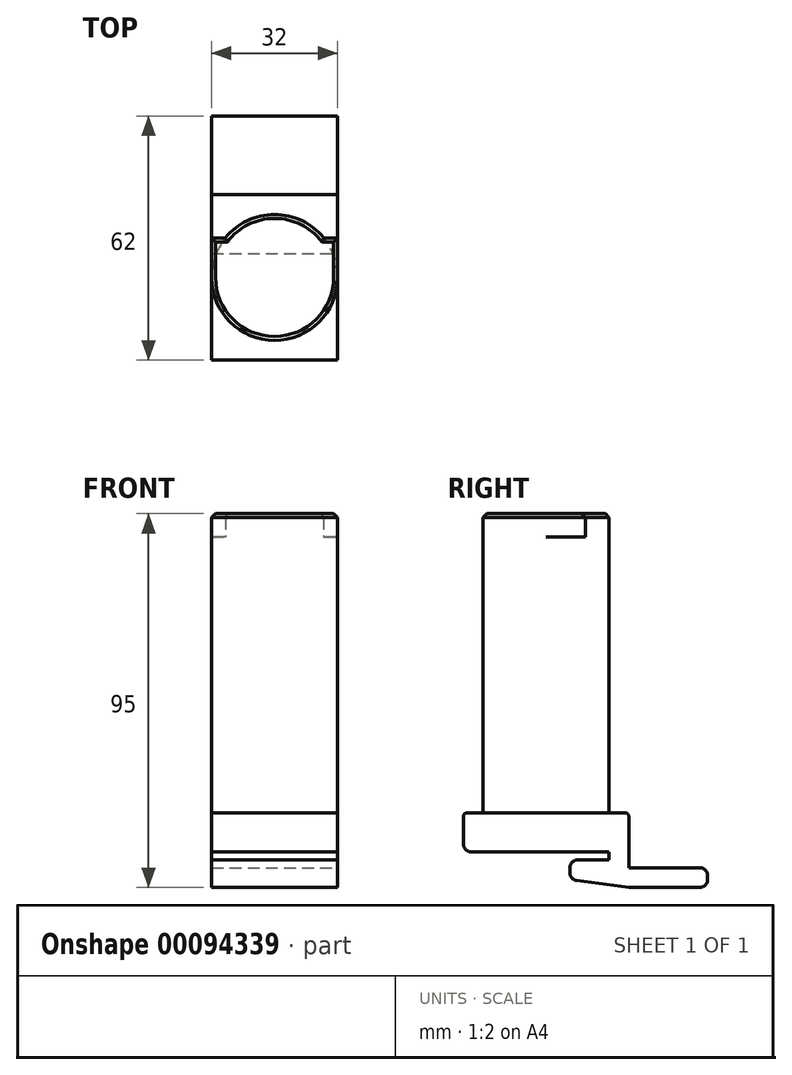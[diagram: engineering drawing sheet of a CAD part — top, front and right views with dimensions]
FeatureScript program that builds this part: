
annotation { "Feature Type Name" : "Feature", "Feature Type Description" : "" }
export const myFeature = defineFeature(function(context is Context, id is Id, definition is map)
    precondition{}
    {
        {
            var Q0;
            Q0=qCreatedBy(makeId("Top.planeOp"),FACE);
            var sketch = newSketch(context, id + "F0", { "sketchPlane" : qUnion([Q0])});
            skCircle(sketch, "E0", {"center": v(0, 0) * mm, "radius": 16 * mm});
            skLineSegment(sketch, "E1.bottom", {"start": v(-16, -21) * mm, "end": v(16, -21) * mm});
            skLineSegment(sketch, "E1.top", {"start": v(-16, 21) * mm, "end": v(16, 21) * mm});
            skLineSegment(sketch, "E1.left", {"start": v(-16, -21) * mm, "end": v(-16, 21) * mm});
            skLineSegment(sketch, "E1.right", {"start": v(16, -21) * mm, "end": v(16, 21) * mm});
            skSolve(sketch);
        }
        {
            var Q0;
            Q0=makeQuery(id+"F0.imprint","IMPRINT",FACE,{"disambiguationData":[TD([[makeQuery(id+"F0.imprint","IMPRINT",EDGE,{"derivedFrom":sQuery(id+"F0.wireOp",EDGE,"E0")}),1.0]])]});
            extrude(context, id + "F1", {"entities" : qUnion([Q0]), "depth" : 70 * mm});
        }
        {
            var Q0;
            Q0=makeQuery(id+"F1.opExtrude","CAP_FACE",FACE,{"disambiguationData":[OSD([sQuery(id+"F0.wireOp",EDGE,"E0")])],"isStart":false});
            var sketch = newSketch(context, id + "F2", { "sketchPlane" : qUnion([Q0])});
            skLineSegment(sketch, "E2", {"start": v(-16, 0) * mm, "end": v(-16, 10) * mm});
            skLineSegment(sketch, "E3", {"start": v(16, 0) * mm, "end": v(16, 10) * mm});
            skLineSegment(sketch, "E4", {"start": v(-16, 10) * mm, "end": v(16, 10) * mm});
            skPoint(sketch, "E5", {"position": v(0, 10) * mm});
            skArc(sketch, "E6", {"start": v(-16, 10) * mm, "mid": v(0, 26) * mm, "end": v(16, 10) * mm});
            skSolve(sketch);
        }
        {
            var Q0;
            {var subQ0=sQuery(id+"F2.wireOp",EDGE,"E6");Q0=makeQuery(id+"F2.imprint","IMPRINT",FACE,{"disambiguationData":[TD([[makeQuery(id+"F2.imprint","IMPRINT",EDGE,{"derivedFrom":subQ0}),-1.0]])]});}
            var Q1;
            {var subQ0=sQuery(id+"F2.wireOp",EDGE,"E4");var subQ1=makeQuery(id+"F1.opExtrude","CAP_EDGE",EDGE,{"disambiguationData":[OSD([sQuery(id+"F0.wireOp",EDGE,"E0")])],"isStart":false});var subQ2=makeQuery(id+"F2.imprint","INTERSECT",VERTEX,{"disambiguationData":[OD(0.0)],"derivedFrom":[subQ1,subQ0]});Q1=makeQuery(id+"F2.imprint","IMPRINT",FACE,{"disambiguationData":[TD([[makeQuery(id+"F2.imprint","IMPRINT",EDGE,{"disambiguationData":[TD([[subQ2,-1.0]])],"derivedFrom":subQ0}),1.0]])]});}
            var Q2;
            {var subQ0=sQuery(id+"F2.wireOp",EDGE,"E2");Q2=makeQuery(id+"F2.imprint","IMPRINT",FACE,{"disambiguationData":[TD([[makeQuery(id+"F2.imprint","IMPRINT",EDGE,{"derivedFrom":subQ0}),-1.0]])]});}
            var Q3;
            {var subQ0=sQuery(id+"F2.wireOp",EDGE,"E3");Q3=makeQuery(id+"F2.imprint","IMPRINT",FACE,{"disambiguationData":[TD([[makeQuery(id+"F2.imprint","IMPRINT",EDGE,{"derivedFrom":subQ0}),1.0]])]});}
            var Q4;
            {var subQ0=sQuery(id+"F2.wireOp",EDGE,"E4");var subQ1=makeQuery(id+"F1.opExtrude","CAP_EDGE",EDGE,{"disambiguationData":[OSD([sQuery(id+"F0.wireOp",EDGE,"E0")])],"isStart":false});var subQ2=makeQuery(id+"F2.imprint","INTERSECT",VERTEX,{"disambiguationData":[OD(0.0)],"derivedFrom":[subQ1,subQ0]});Q4=makeQuery(id+"F2.imprint","IMPRINT",FACE,{"disambiguationData":[TD([[makeQuery(id+"F2.imprint","IMPRINT",EDGE,{"disambiguationData":[TD([[subQ2,-1.0]])],"derivedFrom":subQ0}),-1.0]])]});}
            extrude(context, id + "F3", {"entities" : qUnion([Q0, Q1, Q2, Q3, Q4]), "operationType" : NewBodyOperationType.ADD, "depth" : 6 * mm});
        }
        {
            var Q0;
            {var subQ5=sQuery(id+"F0.wireOp",EDGE,"E1.top");Q0=makeQuery(id+"F0.imprint","IMPRINT",FACE,{"disambiguationData":[TD([[makeQuery(id+"F0.imprint","IMPRINT",EDGE,{"derivedFrom":subQ5}),-1.0]])]});}
            var Q1;
            {var subQ0=sQuery(id+"F0.wireOp",EDGE,"E0");var subQ1=makeQuery(id+"F0.imprint","INTERSECT",VERTEX,{"derivedFrom":[subQ0,sQuery(id+"F0.wireOp",EDGE,"E1.left")]});Q1=makeQuery(id+"F0.imprint","IMPRINT",FACE,{"disambiguationData":[TD([[makeQuery(id+"F0.imprint","IMPRINT",EDGE,{"disambiguationData":[TD([[subQ1,1.0]])],"derivedFrom":subQ0}),1.0]])]});}
            var Q2;
            {var subQ5=sQuery(id+"F0.wireOp",EDGE,"E1.bottom");Q2=makeQuery(id+"F0.imprint","IMPRINT",FACE,{"disambiguationData":[TD([[makeQuery(id+"F0.imprint","IMPRINT",EDGE,{"derivedFrom":subQ5}),1.0]])]});}
            extrude(context, id + "F4", {"entities" : qUnion([Q0, Q1, Q2]), "operationType" : NewBodyOperationType.ADD, "oppositeDirection" : true, "depth" : 10 * mm});
        }
        {
            var Q0;
            Q0=makeQuery(id+"F3.opExtrude","CAP_FACE",FACE,{"disambiguationData":[OSD([sQuery(id+"F0.wireOp",EDGE,"E0"),sQuery(id+"F2.wireOp",EDGE,"E2"),sQuery(id+"F2.wireOp",EDGE,"E3"),sQuery(id+"F2.wireOp",EDGE,"E6")])],"isStart":false});
            var Q1;
            Q1=makeQuery(id+"F3.opExtrude","CAP_EDGE",EDGE,{"disambiguationData":[OSD([sQuery(id+"F2.wireOp",EDGE,"E6")])],"isStart":true});
            chamfer(context, id + "F5", {"entities" : qUnion([Q0, Q1]), "width" : 1 * mm, "tangentPropagation" : true});
        }
        {
            var Q0;
            Q0=makeQuery(id+"F4.opExtrude","SWEPT_FACE",FACE,{"disambiguationData":[OSD([sQuery(id+"F0.wireOp",EDGE,"E1.right")])]});
            var sketch = newSketch(context, id + "F6", { "sketchPlane" : qUnion([Q0])});
            skLineSegment(sketch, "E7.bottom", {"start": v(21, -10) * mm, "end": v(16, -10) * mm});
            skLineSegment(sketch, "E7.top", {"start": v(21, -17) * mm, "end": v(16, -17) * mm});
            skLineSegment(sketch, "E7.left", {"start": v(21, -10) * mm, "end": v(21, -17) * mm});
            skLineSegment(sketch, "E7.right", {"start": v(16, -10) * mm, "end": v(16, -17) * mm});
            skLineSegment(sketch, "E8.bottom", {"start": v(16, -17) * mm, "end": v(6, -17) * mm});
            skLineSegment(sketch, "E8.top", {"start": v(16, -12) * mm, "end": v(6, -12) * mm});
            skLineSegment(sketch, "E8.left", {"start": v(16, -17) * mm, "end": v(16, -12) * mm});
            skLineSegment(sketch, "E8.right", {"start": v(6, -17) * mm, "end": v(6, -12) * mm});
            skLineSegment(sketch, "E9", {"start": v(21, -14) * mm, "end": v(41, -14) * mm});
            skLineSegment(sketch, "E10", {"start": v(41, -14) * mm, "end": v(41, -19) * mm});
            skLineSegment(sketch, "E11", {"start": v(41, -19) * mm, "end": v(21, -19) * mm});
            skLineSegment(sketch, "E12", {"start": v(21, -19) * mm, "end": v(6, -17) * mm});
            skSolve(sketch);
        }
        {
            var Q0;
            {var subQ3=sQuery(id+"F6.wireOp",EDGE,"E7.bottom");Q0=makeQuery(id+"F6.imprint","IMPRINT",FACE,{"disambiguationData":[TD([[makeQuery(id+"F6.imprint","IMPRINT",EDGE,{"derivedFrom":subQ3}),-1.0]])]});}
            var Q1;
            Q1=makeQuery(id+"F6.imprint","IMPRINT",FACE,{"disambiguationData":[TD([[makeQuery(id+"F6.imprint","IMPRINT",EDGE,{"derivedFrom":sQuery(id+"F6.wireOp",EDGE,"E8.bottom")}),-1.0]])]});
            var Q2;
            {var subQ1=sQuery(id+"F6.wireOp",EDGE,"E7.top");Q2=makeQuery(id+"F6.imprint","IMPRINT",FACE,{"disambiguationData":[TD([[makeQuery(id+"F6.imprint","IMPRINT",EDGE,{"derivedFrom":subQ1}),1.0]])]});}
            extrude(context, id + "F7", {"entities" : qUnion([Q0, Q1, Q2]), "operationType" : NewBodyOperationType.ADD, "oppositeDirection" : true, "depth" : 32 * mm});
        }
        {
            var Q0;
            Q0=makeQuery(id+"F4.opExtrude","CAP_EDGE",EDGE,{"disambiguationData":[OSD([sQuery(id+"F0.wireOp",EDGE,"E1.top")])],"isStart":true});
            var Q1;
            Q1=makeQuery(id+"F4.opExtrude","CAP_EDGE",EDGE,{"disambiguationData":[OSD([sQuery(id+"F0.wireOp",EDGE,"E1.bottom")])],"isStart":true});
            fillet(context, id + "F8", {"entities" : qUnion([Q0, Q1]), "radius" : 1 * mm, "tangentPropagation" : true, "allowEdgeOverflow" : false});
        }
        {
            var Q0;
            Q0=makeQuery(id+"F7.opExtrude","SWEPT_EDGE",EDGE,{"disambiguationData":[OSD([sQuery(id+"F6.wireOp",EDGE,"E9"),sQuery(id+"F6.wireOp",EDGE,"E10")])]});
            var Q1;
            Q1=makeQuery(id+"F7.opExtrude","SWEPT_EDGE",EDGE,{"disambiguationData":[OSD([sQuery(id+"F6.wireOp",EDGE,"E10"),sQuery(id+"F6.wireOp",EDGE,"E11")])]});
            var Q2;
            Q2=makeQuery(id+"F7.opExtrude","SWEPT_EDGE",EDGE,{"disambiguationData":[OSD([sQuery(id+"F6.wireOp",EDGE,"E8.bottom"),sQuery(id+"F6.wireOp",EDGE,"E8.right"),sQuery(id+"F6.wireOp",EDGE,"E12")])]});
            var Q3;
            Q3=makeQuery(id+"F7.opExtrude","SWEPT_EDGE",EDGE,{"disambiguationData":[OSD([sQuery(id+"F6.wireOp",EDGE,"E8.top"),sQuery(id+"F6.wireOp",EDGE,"E8.right")])]});
            var Q4;
            Q4=makeQuery(id+"F4.opExtrude","CAP_EDGE",EDGE,{"disambiguationData":[OSD([sQuery(id+"F0.wireOp",EDGE,"E1.bottom")])],"isStart":false});
            fillet(context, id + "F9", {"entities" : qUnion([Q0, Q1, Q2, Q3, Q4]), "radius" : 2 * mm, "tangentPropagation" : true, "allowEdgeOverflow" : false});
        }
    });
